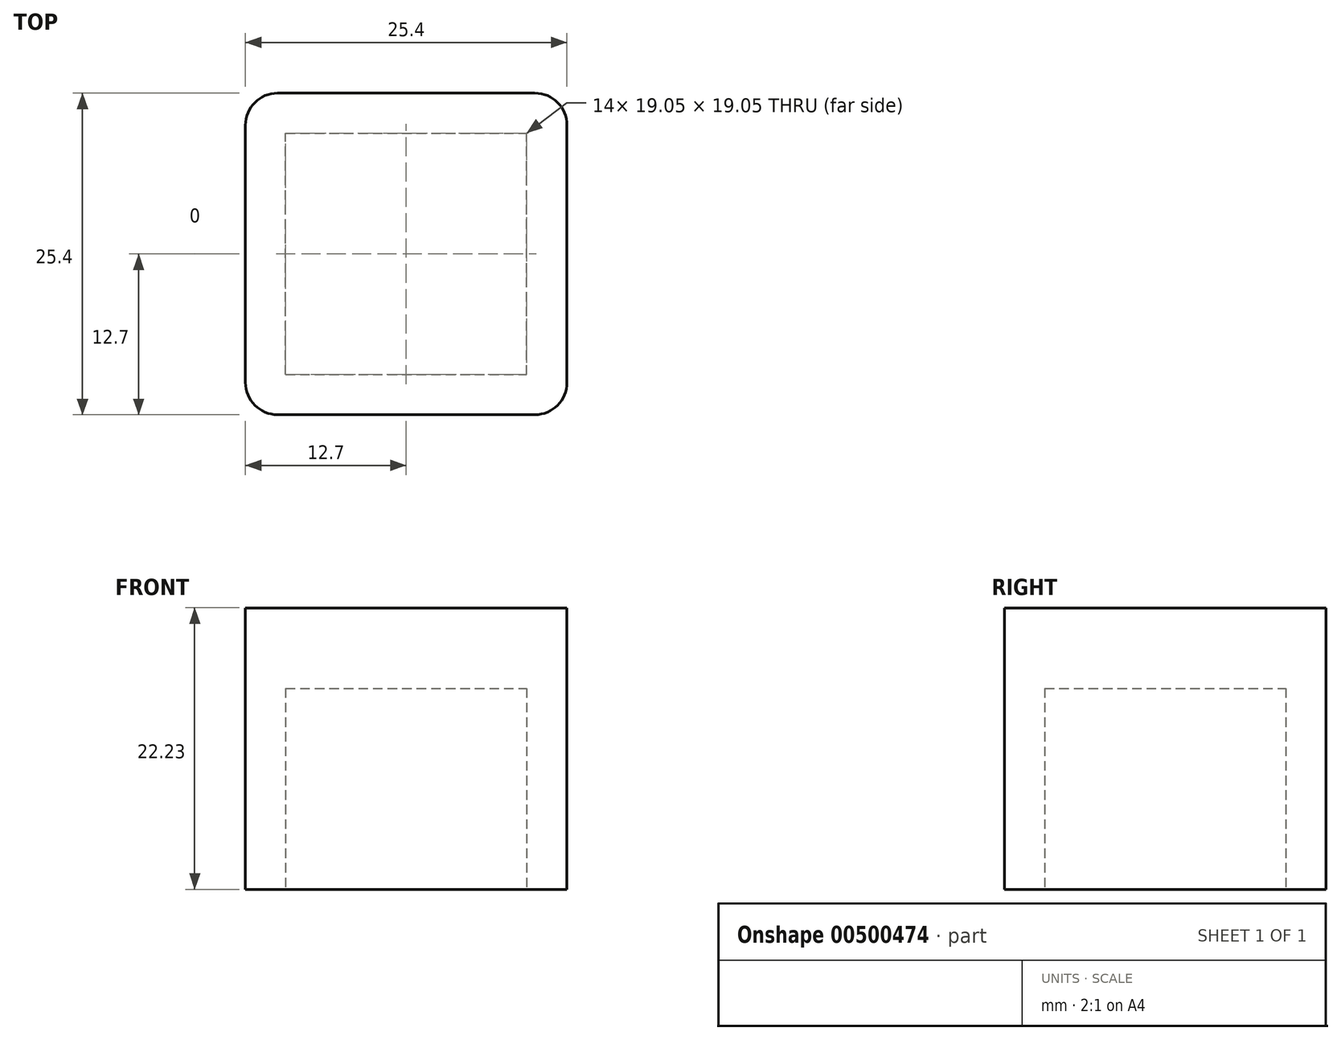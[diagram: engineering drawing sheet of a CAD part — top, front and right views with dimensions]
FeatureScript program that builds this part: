
annotation { "Feature Type Name" : "Feature", "Feature Type Description" : "" }
export const myFeature = defineFeature(function(context is Context, id is Id, definition is map)
    precondition{}
    {
        {
            var Q0;
            Q0=qCreatedBy(makeId("Top.planeOp"),FACE);
            var sketch = newSketch(context, id + "F0", { "sketchPlane" : qUnion([Q0])});
            skLineSegment(sketch, "E0.bottom", {"start": v(0, 25.4) * mm, "end": v(25.4, 25.4) * mm});
            skLineSegment(sketch, "E0.top", {"start": v(0, 0) * mm, "end": v(25.4, 0) * mm});
            skLineSegment(sketch, "E0.left", {"start": v(0, 25.4) * mm, "end": v(0, 0) * mm});
            skLineSegment(sketch, "E0.right", {"start": v(25.4, 25.4) * mm, "end": v(25.4, 0) * mm});
            skSolve(sketch);
        }
        {
            var Q0;
            Q0 = qSketchRegion(id + "F0", true);
            extrude(context, id + "F1", {"entities" : qUnion([Q0]), "depth" : 22.22 * mm, "offsetDistance" : 25.4 * mm});
        }
        {
            var Q0;
            Q0=makeQuery(id+"F1.opExtrude","CAP_FACE",FACE,{"disambiguationData":[OSD([sQuery(id+"F0.wireOp",EDGE,"E0.bottom"),sQuery(id+"F0.wireOp",EDGE,"E0.top"),sQuery(id+"F0.wireOp",EDGE,"E0.left"),sQuery(id+"F0.wireOp",EDGE,"E0.right")])],"isStart":true});
            var sketch = newSketch(context, id + "F2", { "sketchPlane" : qUnion([Q0])});
            skLineSegment(sketch, "E1.bottom", {"start": v(3.17, -22.23) * mm, "end": v(22.22, -22.23) * mm});
            skLineSegment(sketch, "E1.top", {"start": v(3.17, -3.18) * mm, "end": v(22.22, -3.18) * mm});
            skLineSegment(sketch, "E1.left", {"start": v(22.22, -3.18) * mm, "end": v(22.22, -22.23) * mm});
            skLineSegment(sketch, "E1.right", {"start": v(3.18, -3.18) * mm, "end": v(3.17, -22.23) * mm});
            skLineSegment(sketch, "E2", {"start": v(0, 0) * mm, "end": v(25.4, -25.4) * mm, "construction": true});
            skLineSegment(sketch, "E3", {"start": v(3.17, -22.23) * mm, "end": v(22.22, -3.18) * mm, "construction": true});
            skPoint(sketch, "E4", {"position": v(12.7, -12.7) * mm});
            skSolve(sketch);
        }
        {
            var Q0;
            Q0 = qSketchRegion(id + "F2", true);
            extrude(context, id + "F3", {"entities" : qUnion([Q0]), "operationType" : NewBodyOperationType.REMOVE, "oppositeDirection" : true, "depth" : 15.88 * mm, "offsetDistance" : 25.4 * mm});
        }
        {
            var Q0;
            Q0=makeQuery(id+"F1.opExtrude","SWEPT_EDGE",EDGE,{"disambiguationData":[OSD([sQuery(id+"F0.wireOp",EDGE,"E0.top"),sQuery(id+"F0.wireOp",EDGE,"E0.right")])]});
            var Q1;
            Q1=makeQuery(id+"F1.opExtrude","SWEPT_EDGE",EDGE,{"disambiguationData":[OSD([sQuery(id+"F0.wireOp",EDGE,"E0.bottom"),sQuery(id+"F0.wireOp",EDGE,"E0.right")])]});
            var Q2;
            Q2=makeQuery(id+"F1.opExtrude","SWEPT_EDGE",EDGE,{"disambiguationData":[OSD([sQuery(id+"F0.wireOp",EDGE,"E0.bottom"),sQuery(id+"F0.wireOp",EDGE,"E0.left")])]});
            var Q3;
            Q3=makeQuery(id+"F1.opExtrude","SWEPT_EDGE",EDGE,{"disambiguationData":[OSD([sQuery(id+"F0.wireOp",EDGE,"E0.top"),sQuery(id+"F0.wireOp",EDGE,"E0.left")])]});
            fillet(context, id + "F4", {"entities" : qUnion([Q0, Q1, Q2, Q3]), "radius" : 2.54 * mm, "tangentPropagation" : true, "allowEdgeOverflow" : false});
        }
    });
